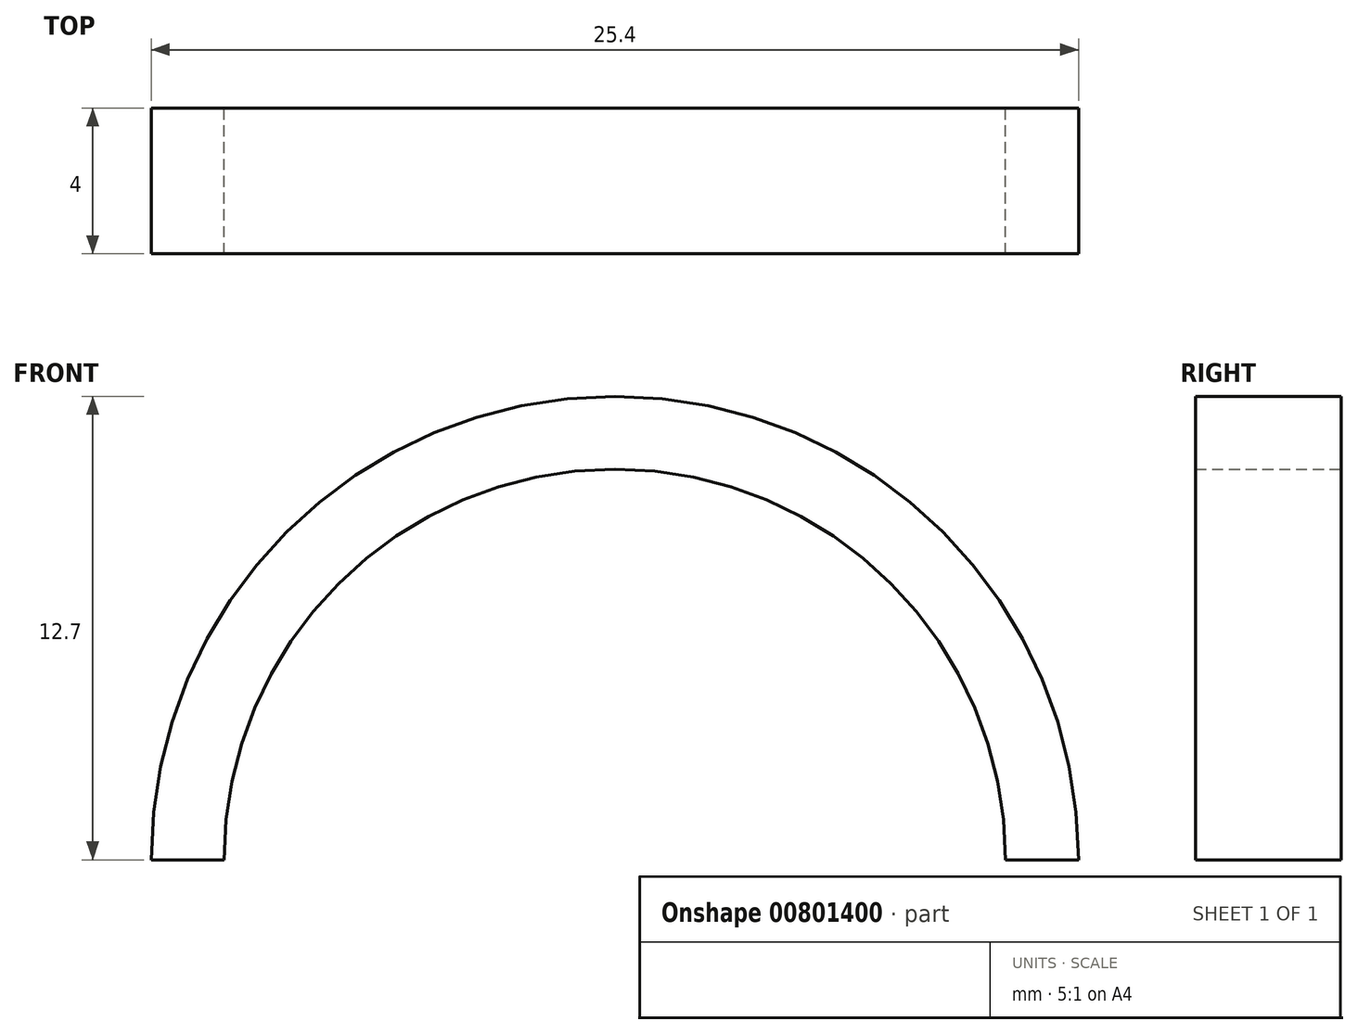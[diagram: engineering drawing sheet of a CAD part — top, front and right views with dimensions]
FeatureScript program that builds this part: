
annotation { "Feature Type Name" : "Feature", "Feature Type Description" : "" }
export const myFeature = defineFeature(function(context is Context, id is Id, definition is map)
    precondition{}
    {
        {
            var Q0;
            Q0=qCreatedBy(makeId("Front.planeOp"),FACE);
            var sketch = newSketch(context, id + "F0", { "sketchPlane" : qUnion([Q0])});
            skArc(sketch, "E0", {"start": v(0, 12.7) * mm, "mid": v(-8.98, 8.98) * mm, "end": v(-12.7, 0) * mm});
            skArc(sketch, "E1", {"start": v(0, 10.7) * mm, "mid": v(-7.57, 7.57) * mm, "end": v(-10.7, 0) * mm});
            skLineSegment(sketch, "E2", {"start": v(0, 12.7) * mm, "end": v(0, 10.7) * mm});
            skLineSegment(sketch, "E3", {"start": v(-10.7, 0) * mm, "end": v(-12.7, 0) * mm});
            skSolve(sketch);
        }
        {
            var Q0;
            Q0 = qSketchRegion(id + "F0", true);
            extrude(context, id + "F1", {"entities" : qUnion([Q0]), "depth" : 2 * mm, "offsetDistance" : 25 * mm, "hasSecondDirection" : true, "secondDirectionOppositeDirection" : true, "secondDirectionDepth" : 2 * mm});
        }
        {
            var Q0;
            Q0=makeQuery(id+"F1.opExtrude","SWEPT_BODY",BODY,{"disambiguationData":[OSD([sQuery(id+"F0.wireOp",EDGE,"E0"),sQuery(id+"F0.wireOp",EDGE,"E1"),sQuery(id+"F0.wireOp",EDGE,"E2"),sQuery(id+"F0.wireOp",EDGE,"E3")])]});
            var Q1;
            Q1=makeQuery(id+"F1.opExtrude","SWEPT_FACE",FACE,{"disambiguationData":[OSD([sQuery(id+"F0.wireOp",EDGE,"E2")])]});
            mirror(context, id + "F2", {"operationType" : NewBodyOperationType.ADD, "entities" : qUnion([Q0]), "mirrorPlane" : qUnion([Q1])});
        }
    });
